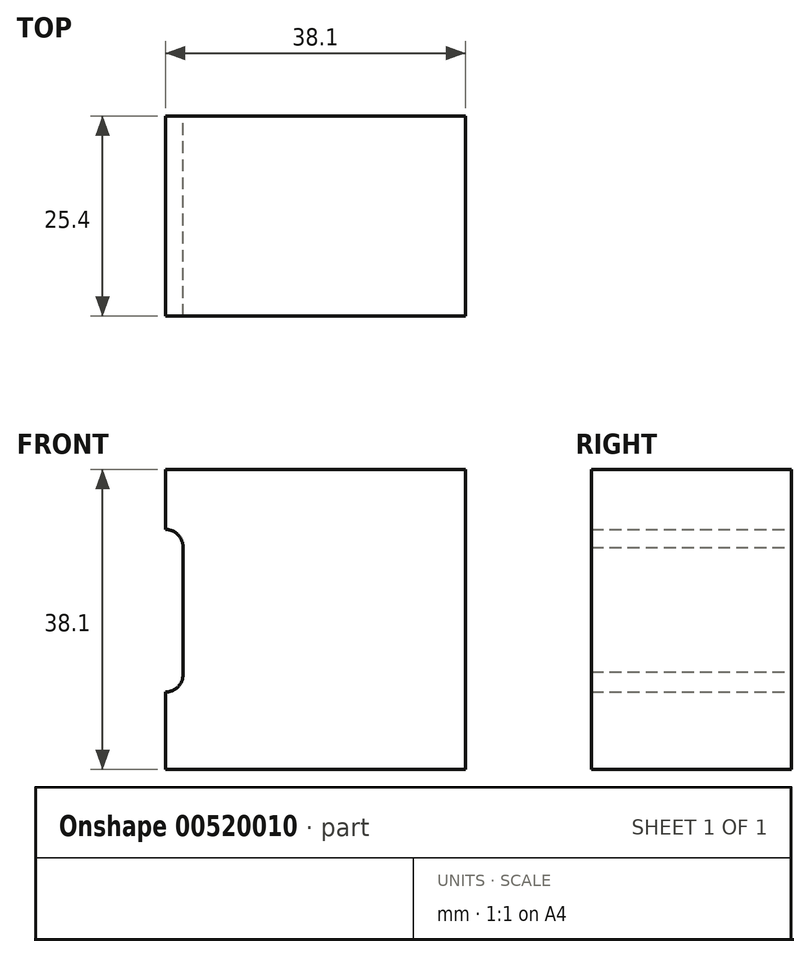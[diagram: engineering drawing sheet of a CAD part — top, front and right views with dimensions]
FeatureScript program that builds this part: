
annotation { "Feature Type Name" : "Feature", "Feature Type Description" : "" }
export const myFeature = defineFeature(function(context is Context, id is Id, definition is map)
    precondition{}
    {
        {
            var Q0;
            Q0=qCreatedBy(makeId("Front.planeOp"),FACE);
            var sketch = newSketch(context, id + "F0", { "sketchPlane" : qUnion([Q0])});
            skLineSegment(sketch, "E0.bottom", {"start": v(0, -19.05) * mm, "end": v(38.1, -19.05) * mm});
            skLineSegment(sketch, "E0.top", {"start": v(0, 19.05) * mm, "end": v(38.1, 19.05) * mm});
            skLineSegment(sketch, "E0.left", {"start": v(0, -19.05) * mm, "end": v(0, 19.05) * mm});
            skLineSegment(sketch, "E0.right", {"start": v(38.1, -19.05) * mm, "end": v(38.1, 19.05) * mm});
            skSolve(sketch);
        }
        {
            var Q0;
            Q0=makeQuery(id+"F0.imprint","IMPRINT",FACE,{"disambiguationData":[TD([[makeQuery(id+"F0.imprint","IMPRINT",EDGE,{"derivedFrom":sQuery(id+"F0.wireOp",EDGE,"E0.bottom")}),1.0]])]});
            extrude(context, id + "F1", {"entities" : qUnion([Q0]), "depth" : 25.4 * mm, "offsetDistance" : 25.4 * mm});
        }
        {
            var Q0;
            Q0=qCreatedBy(makeId("Front.planeOp"),FACE);
            var sketch = newSketch(context, id + "F2", { "sketchPlane" : qUnion([Q0])});
            skLineSegment(sketch, "E1.0", {"start": v(0, 19.05) * mm, "end": v(38.1, 19.05) * mm});
            skArc(sketch, "E2", {"start": v(2.22, 9.18) * mm, "mid": v(1.58, 10.77) * mm, "end": v(0, 11.43) * mm});
            skArc(sketch, "E3", {"start": v(0, -9.2) * mm, "mid": v(1.68, -8.44) * mm, "end": v(2.2, -6.66) * mm});
            skLineSegment(sketch, "E4.0", {"start": v(0, -19.05) * mm, "end": v(38.1, -19.05) * mm});
            skLineSegment(sketch, "E5", {"start": v(2.22, 9.23) * mm, "end": v(2.2, -6.66) * mm});
            skLineSegment(sketch, "E6", {"start": v(0, 11.43) * mm, "end": v(0, -9.2) * mm});
            skSolve(sketch);
        }
        {
            var Q0;
            Q0 = qSketchRegion(id + "F2", true);
            extrude(context, id + "F3", {"entities" : qUnion([Q0]), "operationType" : NewBodyOperationType.REMOVE, "endBound" : BoundingType.THROUGH_ALL, "depth" : 25.4 * mm, "offsetDistance" : 25.4 * mm});
        }
    });
